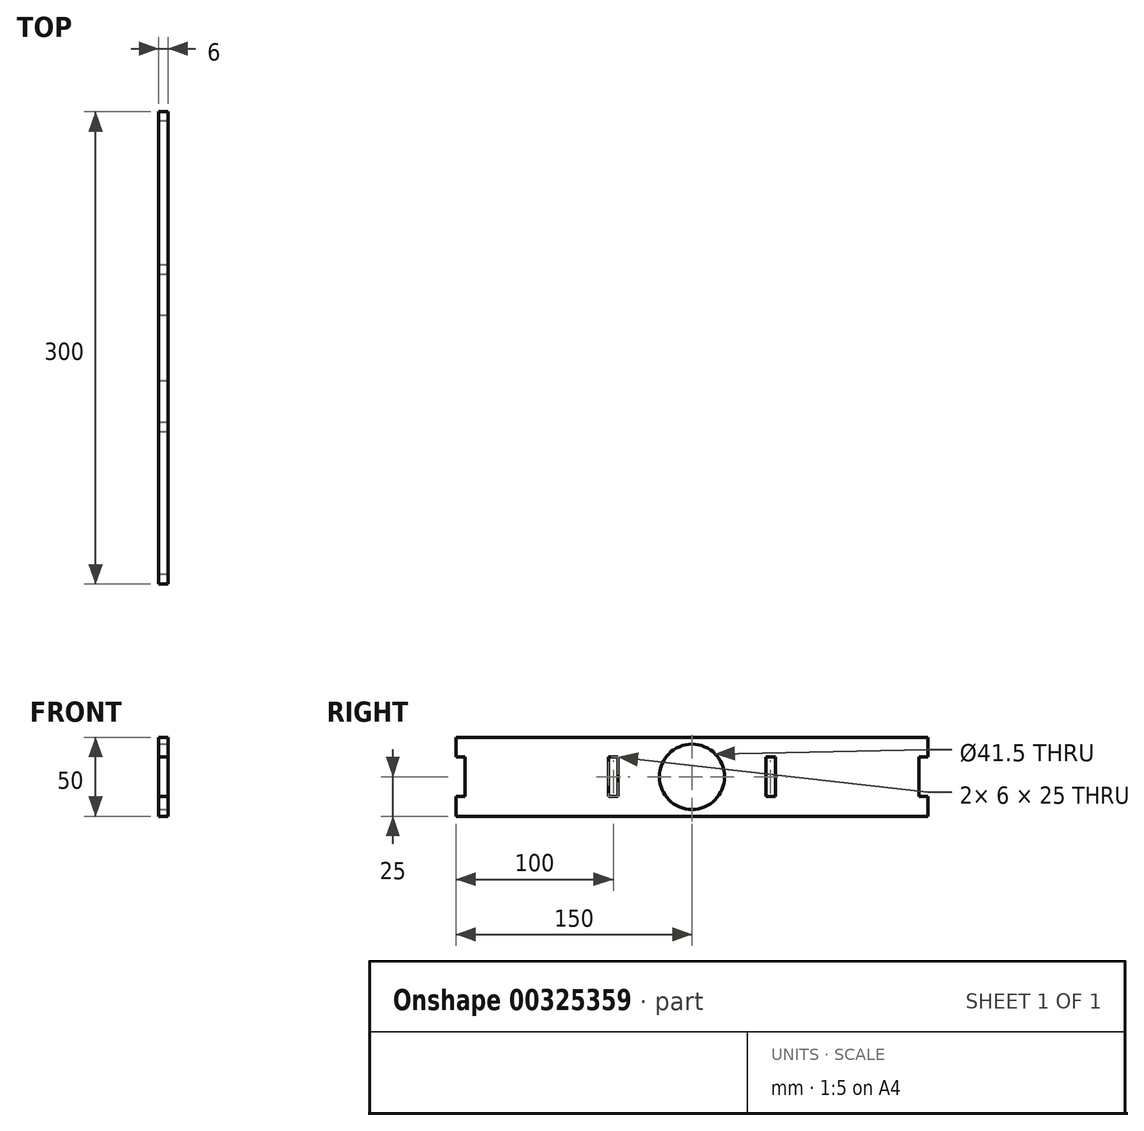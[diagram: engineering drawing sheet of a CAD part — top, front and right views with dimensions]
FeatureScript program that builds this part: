
annotation { "Feature Type Name" : "Feature", "Feature Type Description" : "" }
export const myFeature = defineFeature(function(context is Context, id is Id, definition is map)
    precondition{}
    {
        {
            var Q0;
            Q0=qCreatedBy(makeId("Right.planeOp"),FACE);
            var sketch = newSketch(context, id + "F0", { "sketchPlane" : qUnion([Q0])});
            skLineSegment(sketch, "E0.bottom", {"start": v(-150, 25) * mm, "end": v(150, 25) * mm});
            skLineSegment(sketch, "E0.top", {"start": v(-150, -25) * mm, "end": v(150, -25) * mm});
            skLineSegment(sketch, "E0.left", {"start": v(-150, 25) * mm, "end": v(-150, -25) * mm});
            skLineSegment(sketch, "E0.right", {"start": v(150, 25) * mm, "end": v(150, -25) * mm});
            skPoint(sketch, "E0.middle", {"position": v(0, 0) * mm});
            skLineSegment(sketch, "E1.bottom", {"start": v(-75, 25) * mm, "end": v(75, 25) * mm});
            skLineSegment(sketch, "E1.top", {"start": v(-75, 19) * mm, "end": v(75, 19) * mm});
            skLineSegment(sketch, "E1.left", {"start": v(-75, 25) * mm, "end": v(-75, 19) * mm});
            skLineSegment(sketch, "E1.right", {"start": v(75, 25) * mm, "end": v(75, 19) * mm});
            skPoint(sketch, "E1.middle", {"position": v(0, 22) * mm});
            skLineSegment(sketch, "E2.bottom", {"start": v(-150, 12.5) * mm, "end": v(-144, 12.5) * mm});
            skLineSegment(sketch, "E2.top", {"start": v(-150, -12.5) * mm, "end": v(-144, -12.5) * mm});
            skLineSegment(sketch, "E2.left", {"start": v(-150, 12.5) * mm, "end": v(-150, -12.5) * mm});
            skLineSegment(sketch, "E2.right", {"start": v(-144, 12.5) * mm, "end": v(-144, -12.5) * mm});
            skPoint(sketch, "E2.middle", {"position": v(-147, 0) * mm});
            skLineSegment(sketch, "E3.bottom", {"start": v(150, 12.5) * mm, "end": v(144, 12.5) * mm});
            skLineSegment(sketch, "E3.top", {"start": v(150, -12.5) * mm, "end": v(144, -12.5) * mm});
            skLineSegment(sketch, "E3.left", {"start": v(150, 12.5) * mm, "end": v(150, -12.5) * mm});
            skLineSegment(sketch, "E3.right", {"start": v(144, 12.5) * mm, "end": v(144, -12.5) * mm});
            skPoint(sketch, "E3.middle", {"position": v(147, 0) * mm});
            skPoint(sketch, "E3.middle.positionSnap0", {"position": v(150, 0) * mm});
            skPoint(sketch, "E3.centerSnap0", {"position": v(150, 0) * mm});
            skLineSegment(sketch, "E4.bottom", {"start": v(-75, -25) * mm, "end": v(75, -25) * mm});
            skLineSegment(sketch, "E4.top", {"start": v(-75, -19) * mm, "end": v(75, -19) * mm});
            skLineSegment(sketch, "E4.left", {"start": v(-75, -25) * mm, "end": v(-75, -19) * mm});
            skLineSegment(sketch, "E4.right", {"start": v(75, -25) * mm, "end": v(75, -19) * mm});
            skPoint(sketch, "E4.middle", {"position": v(0, -22) * mm});
            skLineSegment(sketch, "E5.top", {"start": v(-75, 31) * mm, "end": v(75, 31) * mm});
            skLineSegment(sketch, "E5.left", {"start": v(-75, 25) * mm, "end": v(-75, 31) * mm});
            skLineSegment(sketch, "E5.right", {"start": v(75, 25) * mm, "end": v(75, 31) * mm});
            skLineSegment(sketch, "E6.top", {"start": v(-75, -31) * mm, "end": v(75, -31) * mm});
            skLineSegment(sketch, "E6.left", {"start": v(-75, -25) * mm, "end": v(-75, -31) * mm});
            skLineSegment(sketch, "E6.right", {"start": v(75, -25) * mm, "end": v(75, -31) * mm});
            skSolve(sketch);
        }
        {
            var Q0;
            Q0=makeQuery(id+"F0.imprint","IMPRINT",FACE,{"disambiguationData":[TD([[makeQuery(id+"F0.imprint","IMPRINT",EDGE,{"derivedFrom":sQuery(id+"F0.wireOp",EDGE,"E1.top")}),-1.0]])]});
            var Q1;
            Q1=makeQuery(id+"F0.imprint","IMPRINT",FACE,{"disambiguationData":[TD([[makeQuery(id+"F0.imprint","IMPRINT",EDGE,{"derivedFrom":sQuery(id+"F0.wireOp",EDGE,"E1.bottom")}),1.0]])]});
            var Q2;
            Q2=makeQuery(id+"F0.imprint","IMPRINT",FACE,{"disambiguationData":[TD([[makeQuery(id+"F0.imprint","IMPRINT",EDGE,{"derivedFrom":sQuery(id+"F0.wireOp",EDGE,"E1.top")}),1.0]])]});
            var Q3;
            Q3=makeQuery(id+"F0.imprint","IMPRINT",FACE,{"disambiguationData":[TD([[makeQuery(id+"F0.imprint","IMPRINT",EDGE,{"derivedFrom":sQuery(id+"F0.wireOp",EDGE,"E4.bottom")}),-1.0]])]});
            var Q4;
            Q4=makeQuery(id+"F0.imprint","IMPRINT",FACE,{"disambiguationData":[TD([[makeQuery(id+"F0.imprint","IMPRINT",EDGE,{"derivedFrom":sQuery(id+"F0.wireOp",EDGE,"E4.top")}),-1.0]])]});
            extrude(context, id + "F1", {"entities" : qUnion([Q0, Q1, Q2, Q3, Q4]), "depth" : 6 * mm});
        }
        {
            var Q0;
            Q0=makeQuery(id+"F1.opExtrude","CAP_FACE",FACE,{"disambiguationData":[OSD([sQuery(id+"F0.wireOp",EDGE,"E0.bottom"),sQuery(id+"F0.wireOp",EDGE,"E0.top"),sQuery(id+"F0.wireOp",EDGE,"E0.left"),sQuery(id+"F0.wireOp",EDGE,"E0.right"),sQuery(id+"F0.wireOp",EDGE,"E2.bottom"),sQuery(id+"F0.wireOp",EDGE,"E2.top"),sQuery(id+"F0.wireOp",EDGE,"E2.right"),sQuery(id+"F0.wireOp",EDGE,"E3.bottom"),sQuery(id+"F0.wireOp",EDGE,"E3.top"),sQuery(id+"F0.wireOp",EDGE,"E3.right"),sQuery(id+"F0.wireOp",EDGE,"E5.top"),sQuery(id+"F0.wireOp",EDGE,"E5.left"),sQuery(id+"F0.wireOp",EDGE,"E5.right"),sQuery(id+"F0.wireOp",EDGE,"E6.top"),sQuery(id+"F0.wireOp",EDGE,"E6.left"),sQuery(id+"F0.wireOp",EDGE,"E6.right")])],"isStart":false});
            var sketch = newSketch(context, id + "F2", { "sketchPlane" : qUnion([Q0])});
            skCircle(sketch, "E7", {"center": v(0, 0) * mm, "radius": 20.75 * mm});
            skSolve(sketch);
        }
        {
            var Q0;
            Q0 = qSketchRegion(id + "F2", true);
            extrude(context, id + "F3", {"entities" : qUnion([Q0]), "operationType" : NewBodyOperationType.REMOVE, "endBound" : BoundingType.UP_TO_NEXT, "oppositeDirection" : true, "depth" : 25 * mm});
        }
        {
            var Q0;
            Q0=makeQuery(id+"F1.opExtrude","CAP_FACE",FACE,{"disambiguationData":[OSD([sQuery(id+"F0.wireOp",EDGE,"E0.bottom"),sQuery(id+"F0.wireOp",EDGE,"E0.top"),sQuery(id+"F0.wireOp",EDGE,"E0.left"),sQuery(id+"F0.wireOp",EDGE,"E0.right"),sQuery(id+"F0.wireOp",EDGE,"E2.bottom"),sQuery(id+"F0.wireOp",EDGE,"E2.top"),sQuery(id+"F0.wireOp",EDGE,"E2.right"),sQuery(id+"F0.wireOp",EDGE,"E3.bottom"),sQuery(id+"F0.wireOp",EDGE,"E3.top"),sQuery(id+"F0.wireOp",EDGE,"E3.right"),sQuery(id+"F0.wireOp",EDGE,"E5.top"),sQuery(id+"F0.wireOp",EDGE,"E5.left"),sQuery(id+"F0.wireOp",EDGE,"E5.right"),sQuery(id+"F0.wireOp",EDGE,"E6.top"),sQuery(id+"F0.wireOp",EDGE,"E6.left"),sQuery(id+"F0.wireOp",EDGE,"E6.right")])],"isStart":false});
            var sketch = newSketch(context, id + "F4", { "sketchPlane" : qUnion([Q0])});
            skLineSegment(sketch, "E8.bottom", {"start": v(-53, 12.5) * mm, "end": v(-47, 12.5) * mm});
            skLineSegment(sketch, "E8.top", {"start": v(-53, -12.5) * mm, "end": v(-47, -12.5) * mm});
            skLineSegment(sketch, "E8.left", {"start": v(-53, 12.5) * mm, "end": v(-53, -12.5) * mm});
            skLineSegment(sketch, "E8.right", {"start": v(-47, 12.5) * mm, "end": v(-47, -12.5) * mm});
            skPoint(sketch, "E8.middle", {"position": v(-50, 0) * mm});
            skLineSegment(sketch, "E9", {"start": v(0, 31) * mm, "end": v(0, -31) * mm});
            skLineSegment(sketch, "E10.MirrorCS", {"start": v(53, -12.5) * mm, "end": v(47, -12.5) * mm});
            skLineSegment(sketch, "E11.MirrorCS", {"start": v(53, 12.5) * mm, "end": v(53, -12.5) * mm});
            skLineSegment(sketch, "E12.MirrorCS", {"start": v(47, 12.5) * mm, "end": v(47, -12.5) * mm});
            skLineSegment(sketch, "E13.MirrorCS", {"start": v(53, 12.5) * mm, "end": v(47, 12.5) * mm});
            skSolve(sketch);
        }
        {
            var Q0;
            Q0 = qSketchRegion(id + "F4", true);
            extrude(context, id + "F5", {"entities" : qUnion([Q0]), "operationType" : NewBodyOperationType.REMOVE, "endBound" : BoundingType.UP_TO_NEXT, "oppositeDirection" : true, "depth" : 25 * mm});
        }
    });
